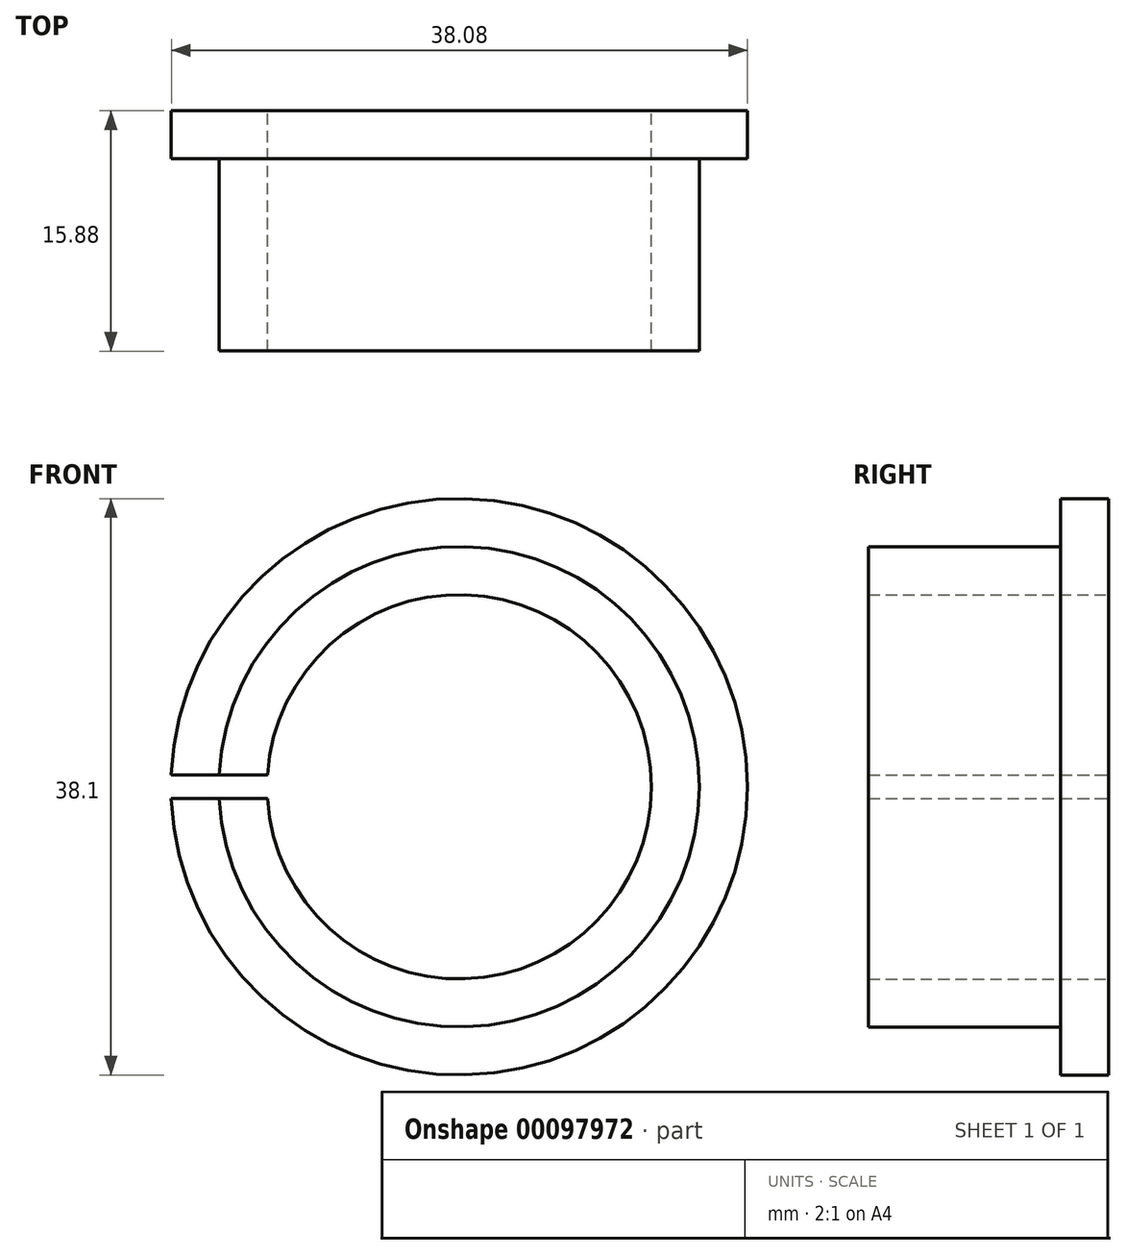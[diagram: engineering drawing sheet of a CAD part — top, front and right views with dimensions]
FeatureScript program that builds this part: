
annotation { "Feature Type Name" : "Feature", "Feature Type Description" : "" }
export const myFeature = defineFeature(function(context is Context, id is Id, definition is map)
    precondition{}
    {
        {
            var Q0;
            Q0=qCreatedBy(makeId("Front.planeOp"),FACE);
            var sketch = newSketch(context, id + "F0", { "sketchPlane" : qUnion([Q0])});
            skCircle(sketch, "E0", {"center": v(0, 0) * mm, "radius": 12.7 * mm});
            skCircle(sketch, "E1", {"center": v(0, 0) * mm, "radius": 15.88 * mm});
            skCircle(sketch, "E2", {"center": v(0, 0) * mm, "radius": 19.05 * mm});
            skSolve(sketch);
        }
        {
            var Q0;
            Q0=makeQuery(id+"F0.imprint","IMPRINT",FACE,{"disambiguationData":[TD([[makeQuery(id+"F0.imprint","IMPRINT",EDGE,{"derivedFrom":sQuery(id+"F0.wireOp",EDGE,"E0")}),-1.0]])]});
            extrude(context, id + "F1", {"entities" : qUnion([Q0]), "depth" : 15.88 * mm});
        }
        {
            var Q0;
            Q0=makeQuery(id+"F0.imprint","IMPRINT",FACE,{"disambiguationData":[TD([[makeQuery(id+"F0.imprint","IMPRINT",EDGE,{"derivedFrom":sQuery(id+"F0.wireOp",EDGE,"E1")}),-1.0]])]});
            extrude(context, id + "F2", {"entities" : qUnion([Q0]), "operationType" : NewBodyOperationType.ADD, "depth" : 3.17 * mm});
        }
        {
            var Q0;
            {var subQ0=sQuery(id+"F0.wireOp",EDGE,"E1");Q0=makeQuery(id+"F2.boolean.opBoolean","MERGE",FACE,{"derivedFrom":[makeQuery(id+"F1.opExtrude","CAP_FACE",FACE,{"disambiguationData":[OSD([sQuery(id+"F0.wireOp",EDGE,"E0"),subQ0])],"isStart":true}),makeQuery(id+"F2.opExtrude","CAP_FACE",FACE,{"disambiguationData":[OSD([subQ0,sQuery(id+"F0.wireOp",EDGE,"E2")])],"isStart":true})]});}
            var sketch = newSketch(context, id + "F3", { "sketchPlane" : qUnion([Q0])});
            skCircle(sketch, "E3.0.0", {"center": v(0, 0) * mm, "radius": 19.05 * mm, "construction": true});
            skLineSegment(sketch, "E4", {"start": v(-19.03, 0.79) * mm, "end": v(19.03, 0.79) * mm, "construction": true});
            skLineSegment(sketch, "E5", {"start": v(-19.03, -0.79) * mm, "end": v(19.03, -0.79) * mm, "construction": true});
            skLineSegment(sketch, "E6", {"start": v(12.68, 0.79) * mm, "end": v(19.03, 0.79) * mm});
            skLineSegment(sketch, "E7", {"start": v(12.68, -0.79) * mm, "end": v(19.03, -0.79) * mm});
            skSolve(sketch);
        }
        {
            var Q0;
            {var subQ0=sQuery(id+"F3.wireOp",EDGE,"E6");Q0=makeQuery(id+"F3.imprint","IMPRINT",FACE,{"disambiguationData":[TD([[makeQuery(id+"F3.imprint","IMPRINT",EDGE,{"derivedFrom":subQ0}),-1.0]])]});}
            extrude(context, id + "F4", {"entities" : qUnion([Q0]), "operationType" : NewBodyOperationType.REMOVE, "endBound" : BoundingType.THROUGH_ALL, "oppositeDirection" : true, "depth" : 25.4 * mm});
        }
    });
